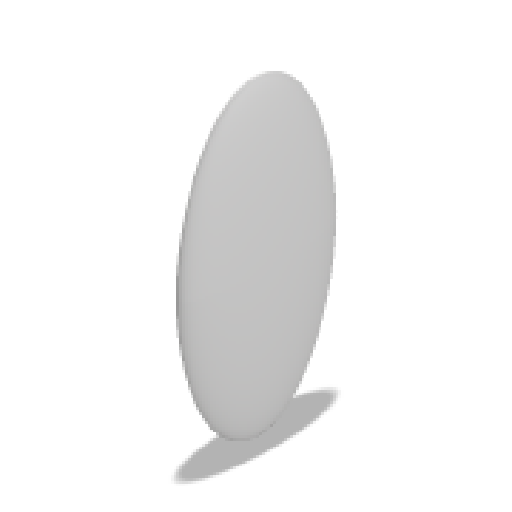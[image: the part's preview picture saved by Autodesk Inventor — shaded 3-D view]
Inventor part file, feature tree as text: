
AUTODESK INVENTOR PART (.ipt)
format: ipt  version: 2023 (Build 270158000, 158)  size: 401,408 bytes
history: native  units: in
note: dims shown in document units (in); Inventor stores cm internally (conversion verified against a paired STEP export)
features: sketch x4, mirror x2, loft x1
ambient origin geometry x8: Origin, YZ Plane, XZ Plane, XY Plane, X Axis, Y Axis, Z Axis, Center Point
bodies: Solid1 (feature_tree)
feature tree (7):
  sketch  "Sketch1"  dims[d0=19.685in d1=4.9213in]
  sketch  "Sketch2"  dims[d2=39.3701in]
  sketch  "Sketch3"  dims[d3=0.0in d4=90.0deg]
  loft  "Loft1"
  mirror  "Mirror1"
  mirror  "Mirror2"
  sketch  "Sketch4"  dims[d5=0.0in d6=90.0deg d7=0.0in d8=90.0deg]
